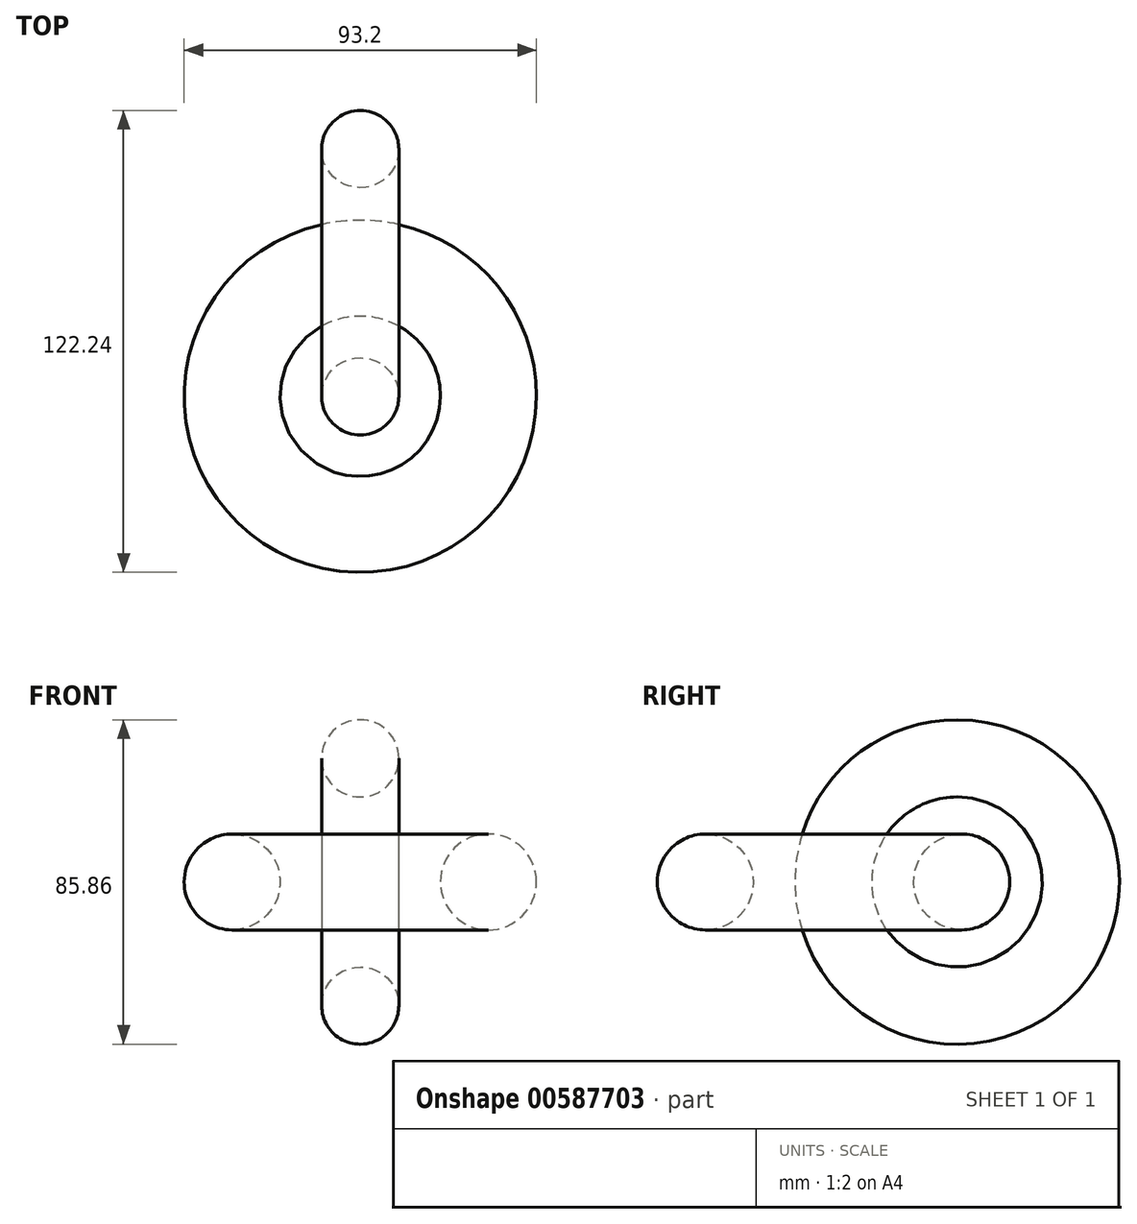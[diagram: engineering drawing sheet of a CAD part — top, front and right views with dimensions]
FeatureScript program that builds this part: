
annotation { "Feature Type Name" : "Feature", "Feature Type Description" : "" }
export const myFeature = defineFeature(function(context is Context, id is Id, definition is map)
    precondition{}
    {
        {
            var Q0;
            Q0=qCreatedBy(makeId("Front.planeOp"),FACE);
            var sketch = newSketch(context, id + "F0", { "sketchPlane" : qUnion([Q0])});
            skLineSegment(sketch, "E0", {"start": v(0, 73.27) * mm, "end": v(0, -45.15) * mm});
            skCircle(sketch, "E1", {"center": v(33.9, 0) * mm, "radius": 12.7 * mm});
            skSolve(sketch);
        }
        {
            var Q0;
            Q0 = qSketchRegion(id + "F0", true);
            var Q1;
            Q1=sQuery(id+"F0.wireOp",EDGE,"E0");
            revolve(context, id + "F1", {"entities" : qUnion([Q0]), "axis" : qUnion([Q1]), "revolveType" : RevolveType.FULL});
        }
        {
            var Q0;
            Q0=qCreatedBy(makeId("Top.planeOp"),FACE);
            var sketch = newSketch(context, id + "F2", { "sketchPlane" : qUnion([Q0])});
            skLineSegment(sketch, "E2", {"start": v(-74.75, 32.71) * mm, "end": v(82.75, 32.71) * mm});
            skCircle(sketch, "E3", {"center": v(0, 0) * mm, "radius": 10.21 * mm});
            skSolve(sketch);
        }
        {
            var Q0;
            Q0 = qSketchRegion(id + "F2", true);
            var Q1;
            Q1=sQuery(id+"F2.wireOp",EDGE,"E2");
            revolve(context, id + "F3", {"entities" : qUnion([Q0]), "axis" : qUnion([Q1]), "revolveType" : RevolveType.FULL});
        }
    });
